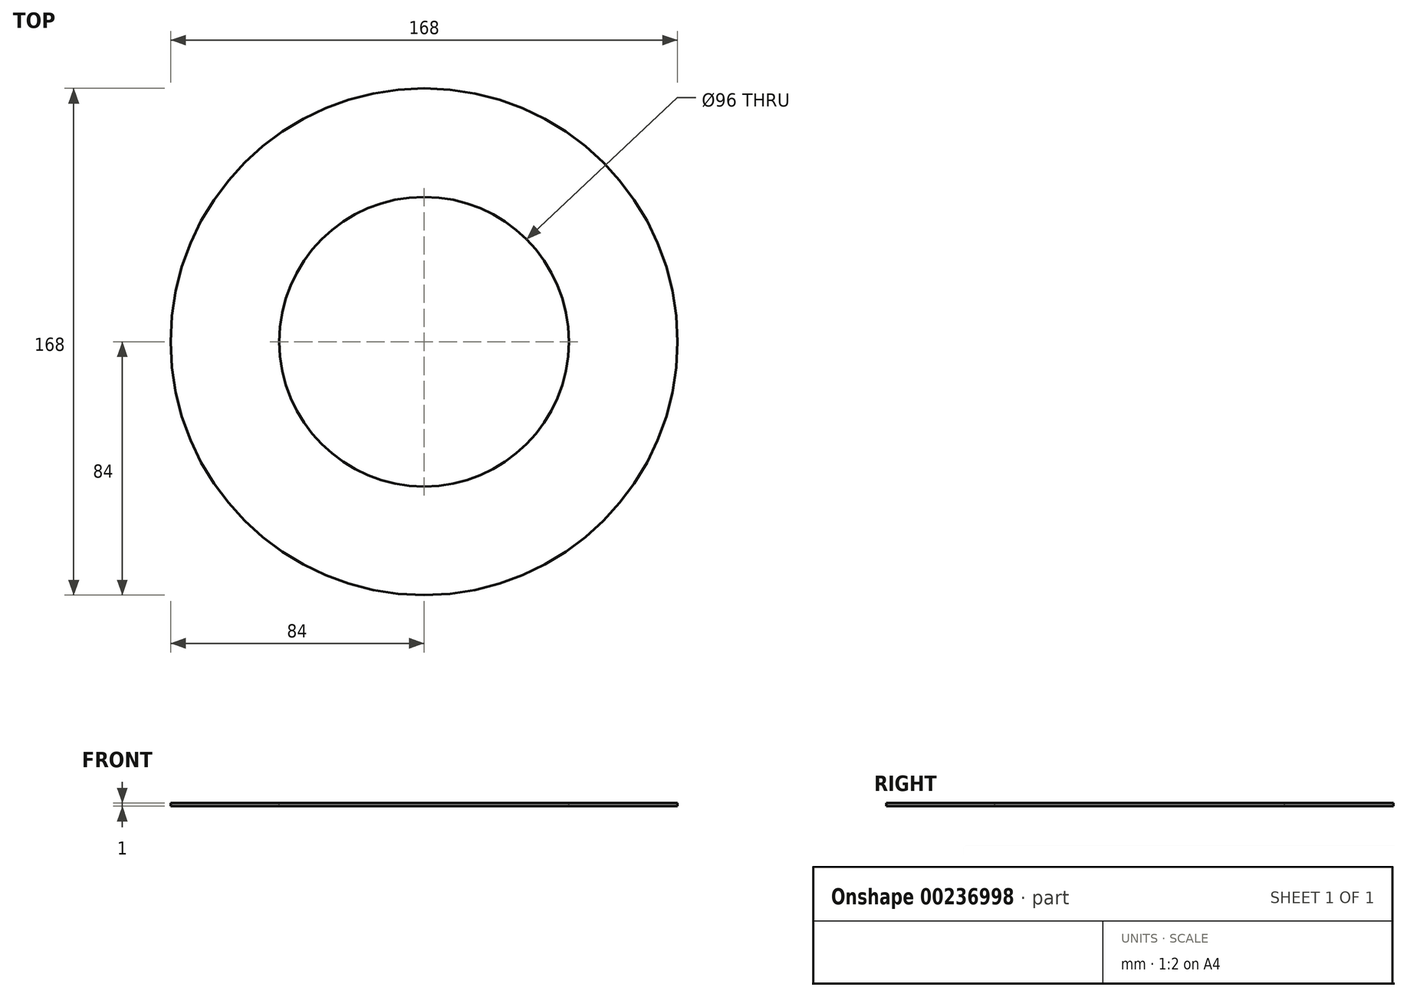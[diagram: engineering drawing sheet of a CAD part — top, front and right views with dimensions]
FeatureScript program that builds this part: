
annotation { "Feature Type Name" : "Feature", "Feature Type Description" : "" }
export const myFeature = defineFeature(function(context is Context, id is Id, definition is map)
    precondition{}
    {
        {
            var Q0;
            Q0=qCreatedBy(makeId("Front.planeOp"),FACE);
            var sketch = newSketch(context, id + "F0", { "sketchPlane" : qUnion([Q0])});
            skLineSegment(sketch, "E0", {"start": v(0, 0) * mm, "end": v(-48, 0) * mm});
            skLineSegment(sketch, "E1.bottom", {"start": v(-48, 0) * mm, "end": v(-84, 0) * mm});
            skLineSegment(sketch, "E1.top", {"start": v(-48, 1) * mm, "end": v(-84, 1) * mm});
            skLineSegment(sketch, "E1.left", {"start": v(-48, 0) * mm, "end": v(-48, 1) * mm});
            skLineSegment(sketch, "E1.right", {"start": v(-84, 0) * mm, "end": v(-84, 1) * mm});
            skLineSegment(sketch, "E2", {"start": v(0, 0) * mm, "end": v(-84, 0) * mm});
            skLineSegment(sketch, "E3", {"start": v(0, 34.49) * mm, "end": v(0, -37.79) * mm, "construction": true});
            skSolve(sketch);
        }
        {
            var Q0;
            Q0=makeQuery(id+"F0.imprint","IMPRINT",FACE,{"disambiguationData":[TD([[makeQuery(id+"F0.imprint","IMPRINT",EDGE,{"derivedFrom":sQuery(id+"F0.wireOp",EDGE,"E1.top")}),1.0]])]});
            var Q1;
            Q1=sQuery(id+"F0.wireOp",EDGE,"E3");
            revolve(context, id + "F1", {"entities" : qUnion([Q0]), "axis" : qUnion([Q1]), "revolveType" : RevolveType.FULL});
        }
    });
